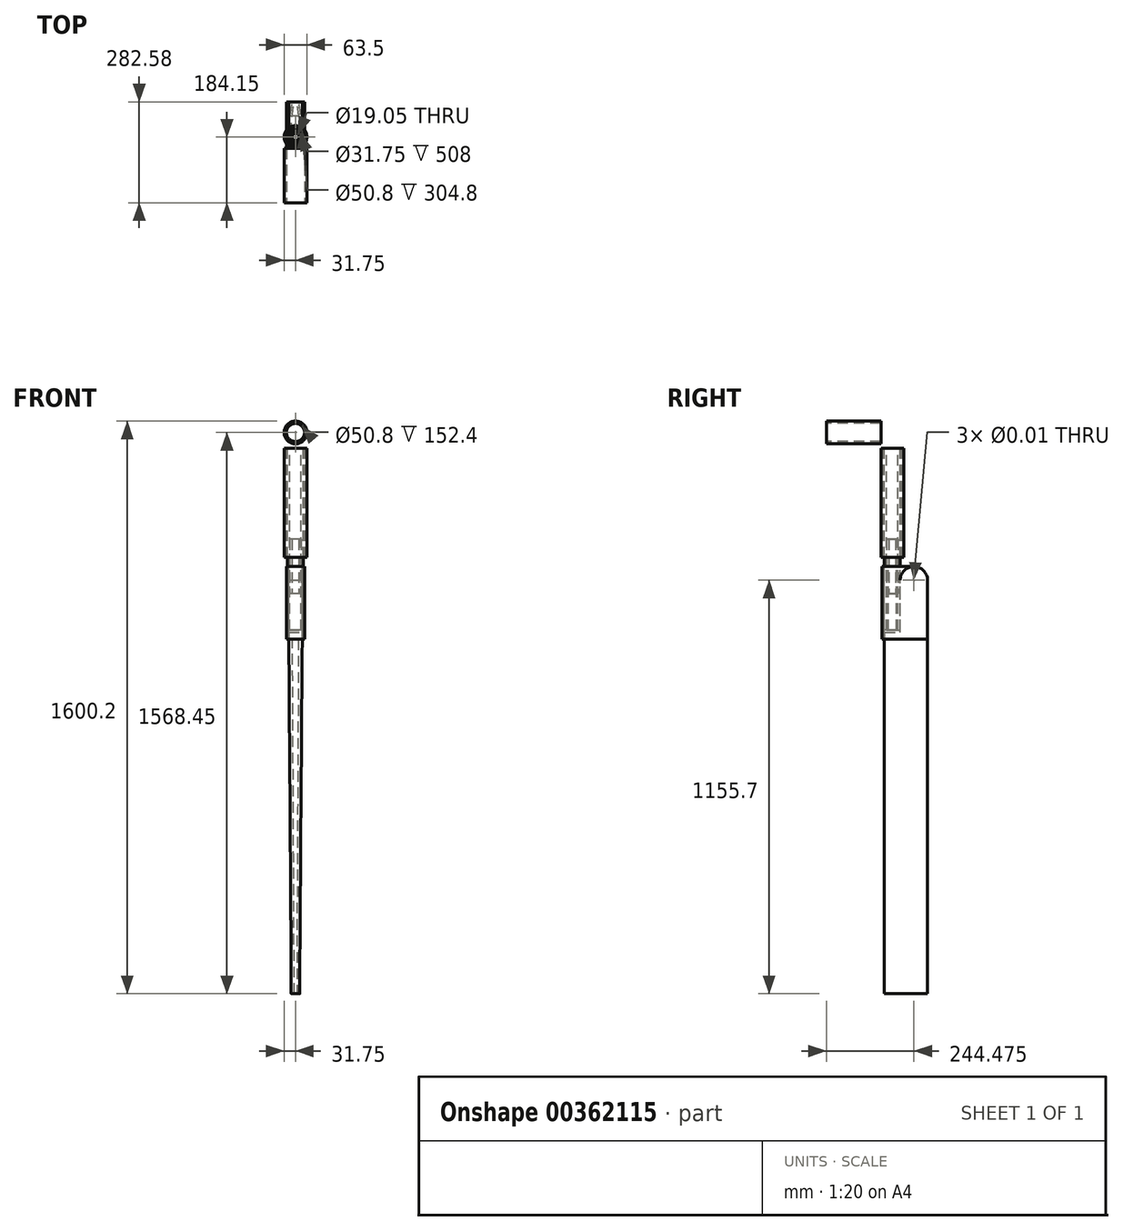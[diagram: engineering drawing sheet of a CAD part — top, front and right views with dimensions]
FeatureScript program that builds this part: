
annotation { "Feature Type Name" : "Feature", "Feature Type Description" : "" }
export const myFeature = defineFeature(function(context is Context, id is Id, definition is map)
    precondition{}
    {
        {
            var Q0;
            Q0=qCreatedBy(makeId("Top.planeOp"),FACE);
            cPlane(context, id + "F0", {"entities" : qUnion([Q0]), "cplaneType" : CPlaneType.OFFSET, "offset" : 609.6 * mm, "oppositeDirection" : true, "width" : 152.4 * mm, "height" : 152.4 * mm});
        }
        {
            var Q0;
            Q0=qCreatedBy(id+"F0.planeOp",FACE);
            cPlane(context, id + "F1", {"entities" : qUnion([Q0]), "cplaneType" : CPlaneType.OFFSET, "offset" : 76.2 * mm, "width" : 152.4 * mm, "height" : 152.4 * mm});
        }
        {
            var Q0;
            Q0=qCreatedBy(id+"F1.planeOp",FACE);
            cPlane(context, id + "F2", {"entities" : qUnion([Q0]), "cplaneType" : CPlaneType.OFFSET, "offset" : 203.2 * mm, "width" : 152.4 * mm, "height" : 152.4 * mm});
        }
        {
            var Q0;
            Q0=qCreatedBy(id+"F2.planeOp",FACE);
            cPlane(context, id + "F3", {"entities" : qUnion([Q0]), "cplaneType" : CPlaneType.OFFSET, "offset" : 25.4 * mm, "width" : 152.4 * mm, "height" : 152.4 * mm});
        }
        {
            var Q0;
            Q0=qCreatedBy(makeId("Front.planeOp"),FACE);
            cPlane(context, id + "F4", {"entities" : qUnion([Q0]), "cplaneType" : CPlaneType.OFFSET, "offset" : 152.4 * mm, "oppositeDirection" : true, "width" : 152.4 * mm, "height" : 152.4 * mm});
        }
        {
            var Q0;
            Q0=qCreatedBy(id+"F0.planeOp",FACE);
            cPlane(context, id + "F5", {"entities" : qUnion([Q0]), "cplaneType" : CPlaneType.OFFSET, "offset" : 914.4 * mm, "oppositeDirection" : true, "width" : 152.4 * mm, "height" : 152.4 * mm});
        }
        {
            var Q0;
            Q0=qCreatedBy(makeId("Front.planeOp"),FACE);
            var sketch = newSketch(context, id + "F6", { "sketchPlane" : qUnion([Q0])});
            skCircle(sketch, "E0", {"center": v(0, 44.45) * mm, "radius": 31.75 * mm});
            skCircle(sketch, "E1", {"center": v(0, 44.45) * mm, "radius": 25.4 * mm});
            skCircle(sketch, "E2", {"center": v(0, 44.45) * mm, "radius": 19.05 * mm});
            skCircle(sketch, "E3", {"center": v(0, 44.45) * mm, "radius": 12.7 * mm});
            skSolve(sketch);
        }
        {
            var Q0;
            Q0=qCreatedBy(makeId("Top.planeOp"),FACE);
            var sketch = newSketch(context, id + "F7", { "sketchPlane" : qUnion([Q0])});
            skCircle(sketch, "E4", {"center": v(0, 184.15) * mm, "radius": 31.75 * mm});
            skCircle(sketch, "E5", {"center": v(0, 184.15) * mm, "radius": 25.4 * mm});
            skCircle(sketch, "E6", {"center": v(0, 184.15) * mm, "radius": 22.23 * mm});
            skCircle(sketch, "E7", {"center": v(0, 184.15) * mm, "radius": 15.88 * mm});
            skSolve(sketch);
        }
        {
            var Q0;
            Q0=makeQuery(id+"F6.imprint","IMPRINT",FACE,{"disambiguationData":[TD([[makeQuery(id+"F6.imprint","IMPRINT",EDGE,{"derivedFrom":sQuery(id+"F6.wireOp",EDGE,"E0")}),1.0]])]});
            var Q1;
            Q1=qCreatedBy(id+"F4.planeOp",FACE);
            extrude(context, id + "F8", {"entities" : qUnion([Q0]), "endBound" : BoundingType.UP_TO_SURFACE, "oppositeDirection" : true, "endBoundEntityFace" : qUnion([Q1]), "depth" : 25.4 * mm});
        }
        {
            var Q0;
            Q0=qCreatedBy(id+"F2.planeOp",FACE);
            var sketch = newSketch(context, id + "F9", { "sketchPlane" : qUnion([Q0])});
            skLineSegment(sketch, "E8.bottom", {"start": v(-25.4, 155.58) * mm, "end": v(25.4, 155.58) * mm});
            skLineSegment(sketch, "E8.left", {"start": v(-25.4, 155.58) * mm, "end": v(-25.4, 282.58) * mm});
            skLineSegment(sketch, "E8.right", {"start": v(25.4, 155.58) * mm, "end": v(25.4, 282.58) * mm});
            skLineSegment(sketch, "E9.0", {"start": v(-19.05, 161.93) * mm, "end": v(-19.05, 282.58) * mm});
            skLineSegment(sketch, "E9.1", {"start": v(-19.05, 161.93) * mm, "end": v(19.05, 161.93) * mm});
            skLineSegment(sketch, "E9.2", {"start": v(19.05, 161.93) * mm, "end": v(19.05, 282.58) * mm});
            skLineSegment(sketch, "E10", {"start": v(-25.4, 282.58) * mm, "end": v(-19.05, 282.58) * mm});
            skLineSegment(sketch, "E11", {"start": v(19.05, 282.58) * mm, "end": v(25.4, 282.58) * mm});
            skCircle(sketch, "E12", {"center": v(0, 184.15) * mm, "radius": 9.53 * mm});
            skCircle(sketch, "E13", {"center": v(0, 184.15) * mm, "radius": 15.88 * mm});
            skSolve(sketch);
        }
        {
            var Q0;
            Q0=makeQuery(id+"F9.imprint","IMPRINT",FACE,{"disambiguationData":[TD([[makeQuery(id+"F9.imprint","IMPRINT",EDGE,{"derivedFrom":sQuery(id+"F9.wireOp",EDGE,"E8.bottom")}),1.0]])]});
            var Q1;
            Q1=qCreatedBy(id+"F1.planeOp",FACE);
            extrude(context, id + "F10", {"entities" : qUnion([Q0]), "endBound" : BoundingType.UP_TO_SURFACE, "oppositeDirection" : true, "endBoundEntityFace" : qUnion([Q1]), "depth" : 25.4 * mm});
        }
        {
            var Q0;
            Q0=makeQuery(id+"F7.imprint","IMPRINT",FACE,{"disambiguationData":[TD([[makeQuery(id+"F7.imprint","IMPRINT",EDGE,{"derivedFrom":sQuery(id+"F7.wireOp",EDGE,"E6")}),1.0]])]});
            extrude(context, id + "F11", {"entities" : qUnion([Q0]), "oppositeDirection" : true, "depth" : 508 * mm});
        }
        {
            var Q0;
            Q0=makeQuery(id+"F10.opExtrude","SWEPT_BODY",BODY,{"disambiguationData":[OSD([sQuery(id+"F9.wireOp",EDGE,"E8.bottom"),sQuery(id+"F9.wireOp",EDGE,"E8.left"),sQuery(id+"F9.wireOp",EDGE,"E8.right"),sQuery(id+"F9.wireOp",EDGE,"E9.0"),sQuery(id+"F9.wireOp",EDGE,"E9.1"),sQuery(id+"F9.wireOp",EDGE,"E9.2"),sQuery(id+"F9.wireOp",EDGE,"E10"),sQuery(id+"F9.wireOp",EDGE,"E11")])]});
            var Q1;
            Q1=makeQuery(id+"F11.opExtrude","SWEPT_BODY",BODY,{"disambiguationData":[OSD([sQuery(id+"F7.wireOp",EDGE,"E6"),sQuery(id+"F7.wireOp",EDGE,"E7")])]});
            booleanBodies(context, id + "F12", {"operationType" : BooleanOperationType.SUBTRACTION, "tools" : qUnion([Q0]), "targets" : qUnion([Q1]), "keepTools" : true});
        }
        {
            var Q0;
            Q0=makeQuery(id+"F9.imprint","IMPRINT",FACE,{"disambiguationData":[TD([[makeQuery(id+"F9.imprint","IMPRINT",EDGE,{"derivedFrom":sQuery(id+"F9.wireOp",EDGE,"E12")}),-1.0]])]});
            extrude(context, id + "F13", {"entities" : qUnion([Q0]), "endBound" : BoundingType.SYMMETRIC, "depth" : 152.4 * mm});
        }
        {
            var Q0;
            Q0=makeQuery(id+"F10.opExtrude","SWEPT_FACE",FACE,{"disambiguationData":[OSD([sQuery(id+"F9.wireOp",EDGE,"E9.2")])]});
            var sketch = newSketch(context, id + "F14", { "sketchPlane" : qUnion([Q0])});
            skCircle(sketch, "E14", {"center": v(-244.48, -368.3) * mm, "radius": 38.1 * mm, "construction": true});
            skLineSegment(sketch, "E15", {"start": v(-206.38, -368.3) * mm, "end": v(-206.38, -514.35) * mm});
            skLineSegment(sketch, "E16", {"start": v(-206.38, -514.35) * mm, "end": v(-161.93, -514.35) * mm});
            skLineSegment(sketch, "E17", {"start": v(-161.93, -514.35) * mm, "end": v(-161.93, -1524) * mm});
            skLineSegment(sketch, "E18", {"start": v(-161.92, -1524) * mm, "end": v(-282.58, -1524) * mm});
            skLineSegment(sketch, "E19", {"start": v(-282.58, -1524) * mm, "end": v(-282.58, -368.3) * mm});
            skArc(sketch, "E20", {"start": v(-282.58, -368.3) * mm, "mid": v(-244.48, -330.2) * mm, "end": v(-206.38, -368.3) * mm});
            skSolve(sketch);
        }
        {
            var Q0;
            {var subQ7=sQuery(id+"F14.wireOp",EDGE,"E15");Q0=makeQuery(id+"F14.imprint","IMPRINT",FACE,{"disambiguationData":[TD([[makeQuery(id+"F14.imprint","IMPRINT",EDGE,{"derivedFrom":subQ7}),-1.0]])]});}
            var Q1;
            {var subQ2=sQuery(id+"F14.wireOp",EDGE,"E18");Q1=makeQuery(id+"F14.imprint","IMPRINT",FACE,{"disambiguationData":[TD([[makeQuery(id+"F14.imprint","IMPRINT",EDGE,{"derivedFrom":subQ2}),-1.0]])]});}
            var Q2;
            Q2=makeQuery(id+"F10.opExtrude","SWEPT_FACE",FACE,{"disambiguationData":[OSD([sQuery(id+"F9.wireOp",EDGE,"E9.0")])]});
            extrude(context, id + "F15", {"entities" : qUnion([Q0, Q1]), "endBound" : BoundingType.UP_TO_SURFACE, "endBoundEntityFace" : qUnion([Q2]), "depth" : 25.4 * mm});
        }
        {
            var Q0;
            Q0=sQuery(id+"F14.wireOp",VERTEX,"E14.center");
            var Q1;
            Q1=makeQuery(id+"F10.opExtrude","SWEPT_BODY",BODY,{"disambiguationData":[OSD([sQuery(id+"F9.wireOp",EDGE,"E8.bottom"),sQuery(id+"F9.wireOp",EDGE,"E8.left"),sQuery(id+"F9.wireOp",EDGE,"E8.right"),sQuery(id+"F9.wireOp",EDGE,"E9.0"),sQuery(id+"F9.wireOp",EDGE,"E9.1"),sQuery(id+"F9.wireOp",EDGE,"E9.2"),sQuery(id+"F9.wireOp",EDGE,"E10"),sQuery(id+"F9.wireOp",EDGE,"E11")])]});
            var Q2;
            Q2=makeQuery(id+"F15.opExtrude","SWEPT_BODY",BODY,{"disambiguationData":[OSD([sQuery(id+"F14.wireOp",EDGE,"E15"),sQuery(id+"F14.wireOp",EDGE,"E16"),sQuery(id+"F14.wireOp",EDGE,"E17"),sQuery(id+"F14.wireOp",EDGE,"E18"),sQuery(id+"F14.wireOp",EDGE,"E19"),sQuery(id+"F14.wireOp",EDGE,"E20")])]});
            hole(context, id + "F16", {"style" : HoleStyle.SIMPLE, "endStyle" : HoleEndStyle.THROUGH, "oppositeDirection" : true, "standardTappedOrClearance" : lookupTablePath({ "standard" : "ANSI", "size" : "3/8 (0.38)", "type" : "Drilled" }), "standardBlindInLast" : lookupTablePath({ "standard" : "ANSI", "size" : "3/8", "type" : "Drilled" }), "holeDiameter" : 3 / 203.2 * mm, "isTappedThrough" : true, "tappedDepth" : 12.7 * mm, "tapClearance" : 3, "locations" : qUnion([Q0]), "scope" : qUnion([Q1, Q2])});
        }
        {
            var Q0;
            Q0=sQuery(id+"F14.wireOp",VERTEX,"E14.center");
            var Q1;
            Q1=makeQuery(id+"F10.opExtrude","SWEPT_BODY",BODY,{"disambiguationData":[OSD([sQuery(id+"F9.wireOp",EDGE,"E8.bottom"),sQuery(id+"F9.wireOp",EDGE,"E8.left"),sQuery(id+"F9.wireOp",EDGE,"E8.right"),sQuery(id+"F9.wireOp",EDGE,"E9.0"),sQuery(id+"F9.wireOp",EDGE,"E9.1"),sQuery(id+"F9.wireOp",EDGE,"E9.2"),sQuery(id+"F9.wireOp",EDGE,"E10"),sQuery(id+"F9.wireOp",EDGE,"E11")])]});
            hole(context, id + "F17", {"style" : HoleStyle.SIMPLE, "endStyle" : HoleEndStyle.THROUGH, "standardTappedOrClearance" : lookupTablePath({ "standard" : "ANSI", "size" : "3/8 (0.38)", "type" : "Drilled" }), "standardBlindInLast" : lookupTablePath({ "standard" : "ANSI", "size" : "3/8", "type" : "Drilled" }), "holeDiameter" : 3 / 203.2 * mm, "isTappedThrough" : true, "tappedDepth" : 12.7 * mm, "tapClearance" : 3, "locations" : qUnion([Q0]), "scope" : qUnion([Q1])});
        }
        {
            var Q0;
            Q0=qCreatedBy(id+"F5.planeOp",FACE);
            var sketch = newSketch(context, id + "F18", { "sketchPlane" : qUnion([Q0])});
            skLineSegment(sketch, "E21.bottom", {"start": v(-76.2, 146.91) * mm, "end": v(76.2, 146.91) * mm});
            skLineSegment(sketch, "E21.top", {"start": v(-76.2, 413.64) * mm, "end": v(76.2, 413.64) * mm});
            skLineSegment(sketch, "E21.left", {"start": v(-76.2, 146.91) * mm, "end": v(-76.2, 413.64) * mm});
            skLineSegment(sketch, "E21.right", {"start": v(76.2, 146.91) * mm, "end": v(76.2, 413.64) * mm});
            skPoint(sketch, "E22.2.internal.snap0", {"position": v(0, 161.93) * mm});
            skPoint(sketch, "E22.3.internal.snap0", {"position": v(0, 161.93) * mm});
            skCircle(sketch, "E23", {"center": v(0, 166.6) * mm, "radius": 4.68 * mm, "construction": true});
            skFitSpline(sketch, "E24", {"points": [v(-4.03, 164.21) * mm, v(-11.86, 201.4) * mm, v(-2.83, 286.87) * mm], "startDerivative": vector(-56.8, 95.47) * mm, "endDerivative": vector(36.37, 217.81) * mm});
            skFitSpline(sketch, "E25.MirrorCS", {"points": [v(4.03, 164.21) * mm, v(11.86, 201.4) * mm, v(2.83, 286.87) * mm], "startDerivative": vector(56.8, 95.47) * mm, "endDerivative": vector(-36.37, 217.81) * mm});
            skArc(sketch, "E26", {"start": v(-4.03, 164.21) * mm, "mid": v(0, 161.93) * mm, "end": v(4.03, 164.21) * mm});
            skLineSegment(sketch, "E27", {"start": v(-2.83, 286.87) * mm, "end": v(2.83, 286.87) * mm});
            skSolve(sketch);
        }
        {
            var Q0;
            Q0=qCreatedBy(id+"F1.planeOp",FACE);
            var sketch = newSketch(context, id + "F19", { "sketchPlane" : qUnion([Q0])});
            skLineSegment(sketch, "E28.bottom", {"start": v(-76.2, 413.64) * mm, "end": v(76.2, 413.64) * mm});
            skLineSegment(sketch, "E28.top", {"start": v(-76.2, 146.91) * mm, "end": v(76.2, 146.91) * mm});
            skLineSegment(sketch, "E28.left", {"start": v(-76.2, 413.64) * mm, "end": v(-76.2, 146.91) * mm});
            skLineSegment(sketch, "E28.right", {"start": v(76.2, 413.64) * mm, "end": v(76.2, 146.91) * mm});
            skCircle(sketch, "E29", {"center": v(0, 166.6) * mm, "radius": 4.68 * mm, "construction": true});
            skFitSpline(sketch, "E30", {"points": [v(-0.48, 161.95) * mm, v(-17.16, 185.3) * mm, v(-6.3, 294.3) * mm], "startDerivative": vector(-68.88, 7.17) * mm, "endDerivative": vector(36.24, 198.23) * mm});
            skFitSpline(sketch, "E31.MirrorCS", {"points": [v(0.48, 161.95) * mm, v(17.16, 185.3) * mm, v(6.3, 294.3) * mm], "startDerivative": vector(68.88, 7.17) * mm, "endDerivative": vector(-36.24, 198.23) * mm});
            skLineSegment(sketch, "E32", {"start": v(-6.3, 294.3) * mm, "end": v(6.3, 294.3) * mm});
            skArc(sketch, "E33", {"start": v(-0.48, 161.95) * mm, "mid": v(0, 161.93) * mm, "end": v(0.48, 161.95) * mm});
            skSolve(sketch);
        }
        {
            var Q0;
            Q0=makeQuery(id+"F19.imprint","IMPRINT",FACE,{"disambiguationData":[TD([[makeQuery(id+"F19.imprint","IMPRINT",EDGE,{"derivedFrom":sQuery(id+"F19.wireOp",EDGE,"E30")}),-1.0]])]});
            var Q1;
            Q1=makeQuery(id+"F18.imprint","IMPRINT",FACE,{"disambiguationData":[TD([[makeQuery(id+"F18.imprint","IMPRINT",EDGE,{"derivedFrom":sQuery(id+"F18.wireOp",EDGE,"E24")}),-1.0]])]});
            loft(context, id + "F20", {"sheetProfilesArray" : [{ "sheetProfileEntities" : qUnion([Q0]) }, { "sheetProfileEntities" : qUnion([Q1]) }]});
        }
        {
            var Q0;
            Q0=makeQuery(id+"F19.imprint","IMPRINT",FACE,{"disambiguationData":[TD([[makeQuery(id+"F19.imprint","IMPRINT",EDGE,{"derivedFrom":sQuery(id+"F19.wireOp",EDGE,"E28.bottom")}),-1.0]])]});
            var Q1;
            Q1=makeQuery(id+"F19.imprint","IMPRINT",FACE,{"disambiguationData":[TD([[makeQuery(id+"F19.imprint","IMPRINT",EDGE,{"derivedFrom":sQuery(id+"F19.wireOp",EDGE,"E30")}),-1.0]])]});
            var Q2;
            Q2=qCreatedBy(id+"F5.planeOp",FACE);
            extrude(context, id + "F21", {"entities" : qUnion([Q0, Q1]), "endBound" : BoundingType.UP_TO_SURFACE, "oppositeDirection" : true, "endBoundEntityFace" : qUnion([Q2]), "depth" : 25.4 * mm});
        }
        {
            var Q0;
            Q0=makeQuery(id+"F20.opLoft","SWEPT_BODY",BODY,{"disambiguationData":[OSD([makeQuery(id+"F18.imprint","IMPRINT",FACE,{"disambiguationData":[TD([[makeQuery(id+"F18.imprint","IMPRINT",EDGE,{"derivedFrom":sQuery(id+"F18.wireOp",EDGE,"E24")}),-1.0]])]}),makeQuery(id+"F19.imprint","IMPRINT",FACE,{"disambiguationData":[TD([[makeQuery(id+"F19.imprint","IMPRINT",EDGE,{"derivedFrom":sQuery(id+"F19.wireOp",EDGE,"E30")}),-1.0]])]})])]});
            var Q1;
            Q1=makeQuery(id+"F21.opExtrude","SWEPT_BODY",BODY,{"disambiguationData":[OSD([sQuery(id+"F19.wireOp",EDGE,"E28.bottom"),sQuery(id+"F19.wireOp",EDGE,"E28.top"),sQuery(id+"F19.wireOp",EDGE,"E28.left"),sQuery(id+"F19.wireOp",EDGE,"E28.right")])]});
            booleanBodies(context, id + "F22", {"operationType" : BooleanOperationType.SUBTRACTION, "tools" : qUnion([Q0]), "targets" : qUnion([Q1])});
        }
        {
            var Q0;
            Q0=makeQuery(id+"F21.opExtrude","SWEPT_BODY",BODY,{"disambiguationData":[OSD([sQuery(id+"F19.wireOp",EDGE,"E28.bottom"),sQuery(id+"F19.wireOp",EDGE,"E28.top"),sQuery(id+"F19.wireOp",EDGE,"E28.left"),sQuery(id+"F19.wireOp",EDGE,"E28.right")])]});
            var Q1;
            Q1=makeQuery(id+"F15.opExtrude","SWEPT_BODY",BODY,{"disambiguationData":[OSD([sQuery(id+"F14.wireOp",EDGE,"E15"),sQuery(id+"F14.wireOp",EDGE,"E16"),sQuery(id+"F14.wireOp",EDGE,"E17"),sQuery(id+"F14.wireOp",EDGE,"E18"),sQuery(id+"F14.wireOp",EDGE,"E19"),sQuery(id+"F14.wireOp",EDGE,"E20")])]});
            booleanBodies(context, id + "F23", {"operationType" : BooleanOperationType.SUBTRACTION, "tools" : qUnion([Q0]), "targets" : qUnion([Q1])});
        }
        {
            var Q0;
            Q0=makeQuery(id+"F7.imprint","IMPRINT",FACE,{"disambiguationData":[TD([[makeQuery(id+"F7.imprint","IMPRINT",EDGE,{"derivedFrom":sQuery(id+"F7.wireOp",EDGE,"E4")}),1.0]])]});
            var Q1;
            Q1=qCreatedBy(id+"F3.planeOp",FACE);
            extrude(context, id + "F24", {"entities" : qUnion([Q0]), "endBound" : BoundingType.UP_TO_SURFACE, "oppositeDirection" : true, "endBoundEntityFace" : qUnion([Q1]), "depth" : 25.4 * mm});
        }
        {
            var Q0;
            {var subQ0=sQuery(id+"F14.wireOp",EDGE,"E20");var subQ1=sQuery(id+"F9.wireOp",EDGE,"E9.2");var subQ4=makeQuery(id+"F10.opExtrude","CAP_EDGE",EDGE,{"disambiguationData":[OSD([subQ1])],"isStart":true});var subQ5=makeQuery(id+"F14.imprint","INTERSECT",VERTEX,{"derivedFrom":[subQ4,subQ0]});Q0=makeQuery(id+"F14.imprint","IMPRINT",FACE,{"disambiguationData":[TD([[makeQuery(id+"F14.imprint","IMPRINT",EDGE,{"disambiguationData":[TD([[subQ5,-1.0]])],"derivedFrom":subQ4}),1.0]])]});}
            extrude(context, id + "F25", {"entities" : qUnion([Q0]), "operationType" : NewBodyOperationType.REMOVE, "endBound" : BoundingType.SYMMETRIC, "depth" : 152.4 * mm});
        }
    });
